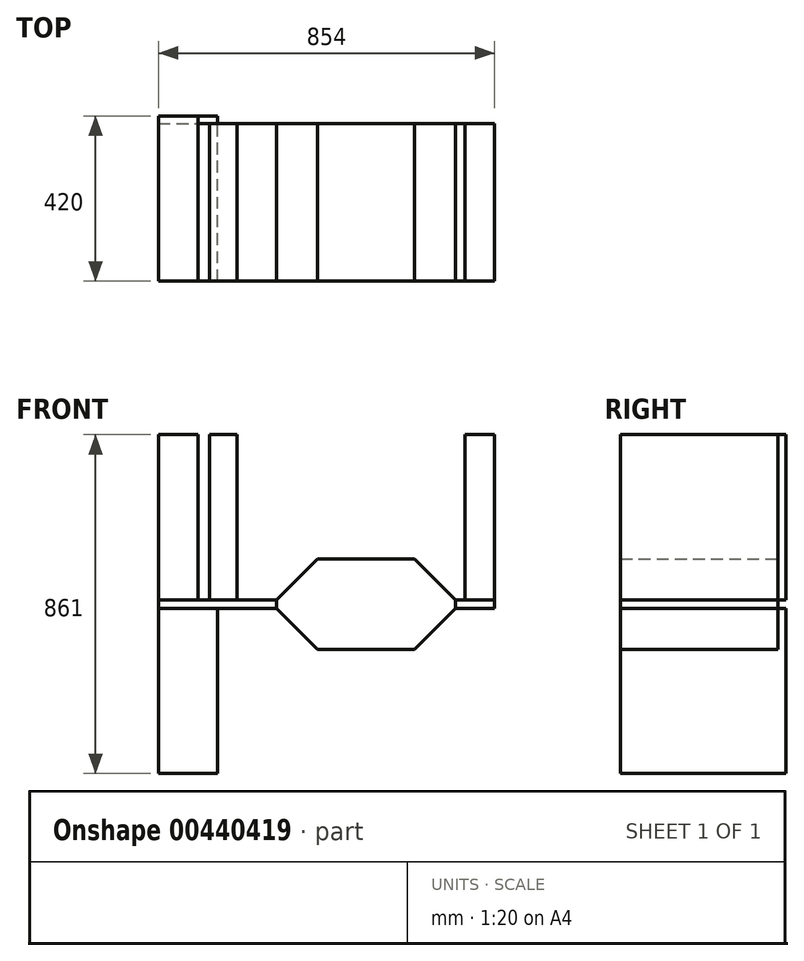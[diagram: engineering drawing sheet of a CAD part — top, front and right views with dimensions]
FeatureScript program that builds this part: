
annotation { "Feature Type Name" : "Feature", "Feature Type Description" : "" }
export const myFeature = defineFeature(function(context is Context, id is Id, definition is map)
    precondition{}
    {
        {
            var Q0;
            Q0=qCreatedBy(makeId("Front.planeOp"),FACE);
            var sketch = newSketch(context, id + "F0", { "sketchPlane" : qUnion([Q0])});
            skLineSegment(sketch, "E0", {"start": v(-124.14, -104.9) * mm, "end": v(-228.18, -0.41) * mm});
            skLineSegment(sketch, "E1", {"start": v(-228.18, -0.41) * mm, "end": v(-228.18, 20.59) * mm});
            skLineSegment(sketch, "E2", {"start": v(-228.18, 20.59) * mm, "end": v(-124.18, 125.1) * mm});
            skLineSegment(sketch, "E3", {"start": v(-124.18, 125.1) * mm, "end": v(121.82, 125.1) * mm});
            skLineSegment(sketch, "E4", {"start": v(121.82, 125.1) * mm, "end": v(225.82, 20.59) * mm});
            skLineSegment(sketch, "E5", {"start": v(225.82, 20.59) * mm, "end": v(225.82, -0.41) * mm});
            skLineSegment(sketch, "E6", {"start": v(225.82, -0.41) * mm, "end": v(121.86, -104.98) * mm});
            skLineSegment(sketch, "E7", {"start": v(121.86, -104.98) * mm, "end": v(-124.14, -104.9) * mm});
            skLineSegment(sketch, "E8", {"start": v(283.33, 10.09) * mm, "end": v(-252.99, 10.09) * mm, "construction": true});
            skPoint(sketch, "E8.startSnap0", {"position": v(225.82, 10.09) * mm});
            skPoint(sketch, "E8.endSnap0", {"position": v(-228.18, 10.09) * mm});
            skPoint(sketch, "E9.endSnap0", {"position": v(-1.14, -104.93) * mm});
            skLineSegment(sketch, "E10", {"start": v(-1.14, -176.84) * mm, "end": v(-1.14, 144.6) * mm, "construction": true});
            skPoint(sketch, "E11", {"position": v(-1.14, 10.09) * mm});
            skSolve(sketch);
        }
        {
            var Q0;
            Q0=makeQuery(id+"F0.imprint","IMPRINT",FACE,{"disambiguationData":[TD([[makeQuery(id+"F0.imprint","IMPRINT",EDGE,{"derivedFrom":sQuery(id+"F0.wireOp",EDGE,"E0")}),-1.0]])]});
            extrude(context, id + "F1", {"entities" : qUnion([Q0]), "depth" : 400 * mm});
        }
        {
            var Q0;
            Q0=makeQuery(id+"F1.opExtrude","SWEPT_FACE",FACE,{"disambiguationData":[OSD([sQuery(id+"F0.wireOp",EDGE,"E5")])]});
            var sketch = newSketch(context, id + "F2", { "sketchPlane" : qUnion([Q0])});
            skSolve(sketch);
        }
        {
            var Q0;
            {var subQ0=sQuery(id+"F0.wireOp",EDGE,"E5");Q0=makeQuery(id+"F2.imprint","IMPRINT",FACE,{"disambiguationData":[TD([[makeQuery(id+"F2.imprint","IMPRINT",EDGE,{"derivedFrom":makeQuery(id+"F1.opExtrude","CAP_EDGE",EDGE,{"disambiguationData":[OSD([subQ0])],"isStart":true})}),-1.0]])]});}
            extrude(context, id + "F3", {"entities" : qUnion([Q0]), "depth" : 100 * mm});
        }
        {
            var Q0;
            Q0=makeQuery(id+"F1.opExtrude","SWEPT_FACE",FACE,{"disambiguationData":[OSD([sQuery(id+"F0.wireOp",EDGE,"E1")])]});
            extrude(context, id + "F4", {"entities" : qUnion([Q0]), "depth" : 300 * mm});
        }
        {
            var Q0;
            Q0=makeQuery(id+"F4.opExtrude","SWEPT_FACE",FACE,{"disambiguationData":[OSD([sQuery(id+"F0.wireOp",EDGE,"E1"),sQuery(id+"F0.wireOp",EDGE,"E2")])]});
            var sketch = newSketch(context, id + "F5", { "sketchPlane" : qUnion([Q0])});
            skLineSegment(sketch, "E12.bottom", {"start": v(-528.18, -400) * mm, "end": v(-428.18, -400) * mm});
            skLineSegment(sketch, "E12.top", {"start": v(-528.18, 20) * mm, "end": v(-428.18, 20) * mm});
            skLineSegment(sketch, "E12.left", {"start": v(-528.18, -400) * mm, "end": v(-528.18, 20) * mm});
            skLineSegment(sketch, "E12.right", {"start": v(-428.18, -400) * mm, "end": v(-428.18, 20) * mm});
            skSolve(sketch);
        }
        {
            var Q0;
            {var subQ0=sQuery(id+"F5.wireOp",EDGE,"E12.top");Q0=makeQuery(id+"F5.imprint","IMPRINT",FACE,{"disambiguationData":[TD([[makeQuery(id+"F5.imprint","IMPRINT",EDGE,{"derivedFrom":subQ0}),-1.0]])]});}
            var Q1;
            {var subQ0=sQuery(id+"F5.wireOp",EDGE,"E12.bottom");Q1=makeQuery(id+"F5.imprint","IMPRINT",FACE,{"disambiguationData":[TD([[makeQuery(id+"F5.imprint","IMPRINT",EDGE,{"derivedFrom":subQ0}),1.0]])]});}
            extrude(context, id + "F6", {"entities" : qUnion([Q0, Q1]), "depth" : 420 * mm});
        }
        {
            var Q0;
            Q0=makeQuery(id+"F4.opExtrude","SWEPT_FACE",FACE,{"disambiguationData":[OSD([sQuery(id+"F0.wireOp",EDGE,"E1"),sQuery(id+"F0.wireOp",EDGE,"E2")])]});
            var sketch = newSketch(context, id + "F7", { "sketchPlane" : qUnion([Q0])});
            skLineSegment(sketch, "E13.bottom", {"start": v(-398.18, 0) * mm, "end": v(-328.18, 0) * mm});
            skLineSegment(sketch, "E13.top", {"start": v(-398.18, -400) * mm, "end": v(-328.18, -400) * mm});
            skLineSegment(sketch, "E13.left", {"start": v(-398.18, 0) * mm, "end": v(-398.18, -400) * mm});
            skLineSegment(sketch, "E13.right", {"start": v(-328.18, 0) * mm, "end": v(-328.18, -400) * mm});
            skSolve(sketch);
        }
        {
            var Q0;
            Q0=makeQuery(id+"F7.imprint","IMPRINT",FACE,{"disambiguationData":[TD([[makeQuery(id+"F7.imprint","IMPRINT",EDGE,{"derivedFrom":sQuery(id+"F7.wireOp",EDGE,"E13.bottom")}),-1.0]])]});
            var Q1;
            Q1=makeQuery(id+"F6.opExtrude","CAP_FACE",FACE,{"disambiguationData":[OSD([sQuery(id+"F5.wireOp",EDGE,"E12.bottom"),sQuery(id+"F5.wireOp",EDGE,"E12.top"),sQuery(id+"F5.wireOp",EDGE,"E12.left"),sQuery(id+"F5.wireOp",EDGE,"E12.right")])],"isStart":false});
            extrude(context, id + "F8", {"entities" : qUnion([Q0]), "endBound" : BoundingType.UP_TO_SURFACE, "endBoundEntityFace" : qUnion([Q1]), "depth" : 25 * mm});
        }
        {
            var Q0;
            Q0=makeQuery(id+"F4.opExtrude","SWEPT_FACE",FACE,{"disambiguationData":[OSD([sQuery(id+"F0.wireOp",EDGE,"E0"),sQuery(id+"F0.wireOp",EDGE,"E1")])]});
            var sketch = newSketch(context, id + "F9", { "sketchPlane" : qUnion([Q0])});
            skPoint(sketch, "E14.0", {"position": v(-528.18, -20) * mm});
            skLineSegment(sketch, "E15.bottom", {"start": v(-528.18, 400) * mm, "end": v(-378.18, 400) * mm});
            skLineSegment(sketch, "E15.top", {"start": v(-528.18, -20) * mm, "end": v(-378.18, -20) * mm});
            skLineSegment(sketch, "E15.left", {"start": v(-528.18, 400) * mm, "end": v(-528.18, -20) * mm});
            skLineSegment(sketch, "E15.right", {"start": v(-378.18, 400) * mm, "end": v(-378.18, -20) * mm});
            skSolve(sketch);
        }
        {
            var Q0;
            {var subQ0=sQuery(id+"F9.wireOp",EDGE,"E15.top");Q0=makeQuery(id+"F9.imprint","IMPRINT",FACE,{"disambiguationData":[TD([[makeQuery(id+"F9.imprint","IMPRINT",EDGE,{"derivedFrom":subQ0}),1.0]])]});}
            var Q1;
            {var subQ0=sQuery(id+"F9.wireOp",EDGE,"E15.bottom");Q1=makeQuery(id+"F9.imprint","IMPRINT",FACE,{"disambiguationData":[TD([[makeQuery(id+"F9.imprint","IMPRINT",EDGE,{"derivedFrom":subQ0}),-1.0]])]});}
            extrude(context, id + "F10", {"entities" : qUnion([Q0, Q1]), "depth" : 420 * mm});
        }
        {
            var Q0;
            Q0=makeQuery(id+"F3.opExtrude","SWEPT_FACE",FACE,{"disambiguationData":[OSD([sQuery(id+"F0.wireOp",EDGE,"E4"),sQuery(id+"F0.wireOp",EDGE,"E5")])]});
            var sketch = newSketch(context, id + "F11", { "sketchPlane" : qUnion([Q0])});
            skLineSegment(sketch, "E16.bottom", {"start": v(325.82, 0) * mm, "end": v(250.82, 0) * mm});
            skLineSegment(sketch, "E16.top", {"start": v(325.82, -400) * mm, "end": v(250.82, -400) * mm});
            skLineSegment(sketch, "E16.left", {"start": v(325.82, 0) * mm, "end": v(325.82, -400) * mm});
            skLineSegment(sketch, "E16.right", {"start": v(250.82, 0) * mm, "end": v(250.82, -400) * mm});
            skSolve(sketch);
        }
        {
            var Q0;
            Q0=makeQuery(id+"F11.imprint","IMPRINT",FACE,{"disambiguationData":[TD([[makeQuery(id+"F11.imprint","IMPRINT",EDGE,{"derivedFrom":sQuery(id+"F11.wireOp",EDGE,"E16.bottom")}),1.0]])]});
            var Q1;
            Q1=makeQuery(id+"F8.opExtrude","CAP_FACE",FACE,{"disambiguationData":[OSD([sQuery(id+"F7.wireOp",EDGE,"E13.bottom"),sQuery(id+"F7.wireOp",EDGE,"E13.top"),sQuery(id+"F7.wireOp",EDGE,"E13.left"),sQuery(id+"F7.wireOp",EDGE,"E13.right")])],"isStart":false});
            extrude(context, id + "F12", {"entities" : qUnion([Q0]), "endBound" : BoundingType.UP_TO_SURFACE, "endBoundEntityFace" : qUnion([Q1]), "depth" : 25 * mm});
        }
    });
